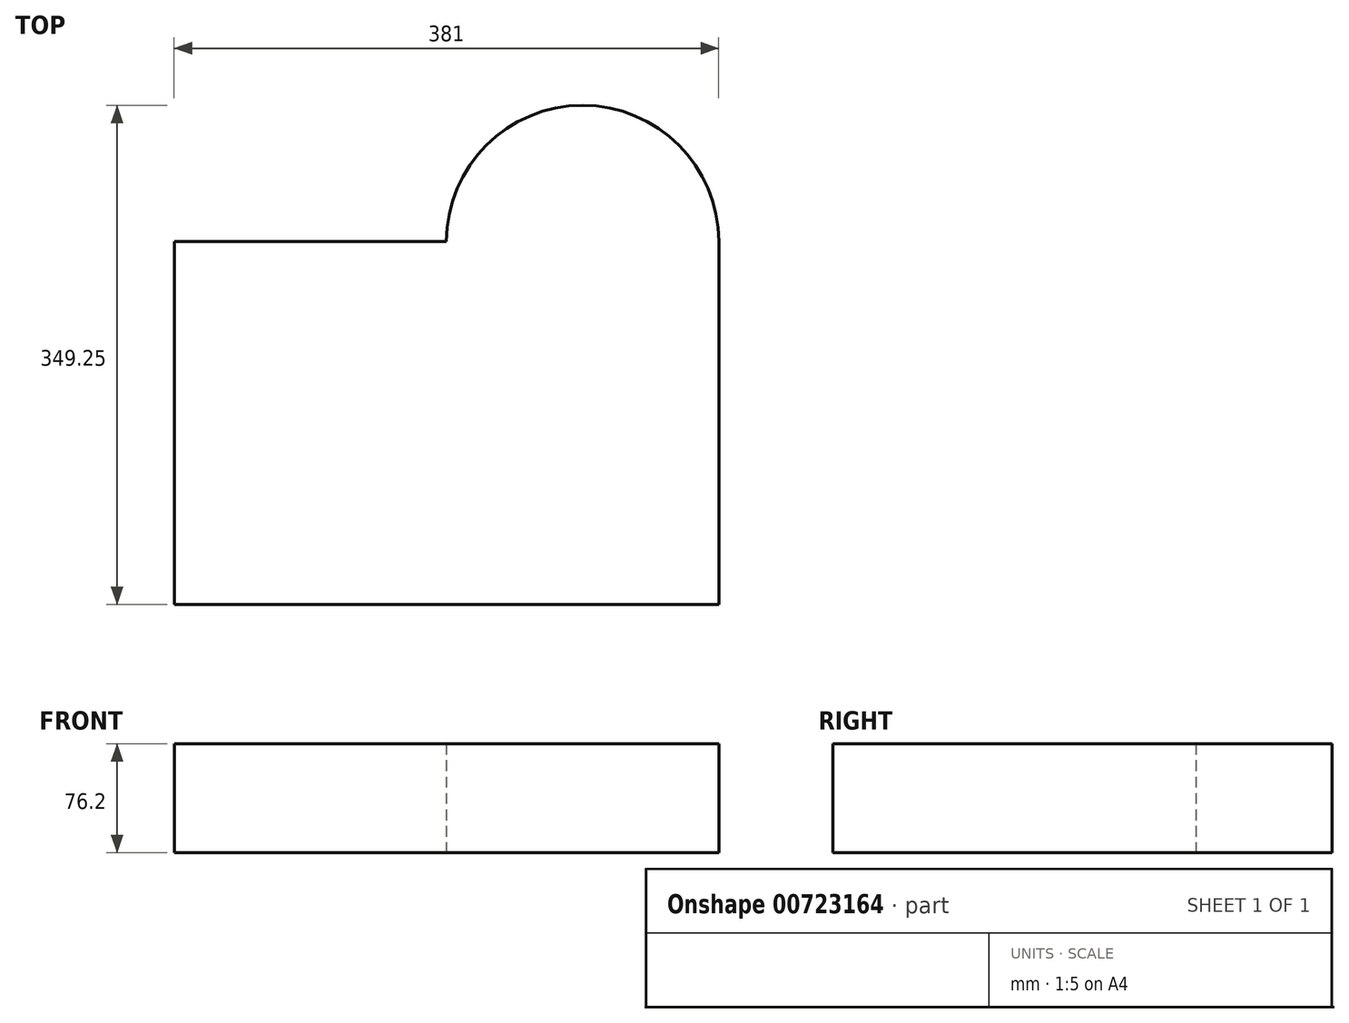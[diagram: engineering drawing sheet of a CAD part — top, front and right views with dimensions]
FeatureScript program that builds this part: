
annotation { "Feature Type Name" : "Feature", "Feature Type Description" : "" }
export const myFeature = defineFeature(function(context is Context, id is Id, definition is map)
    precondition{}
    {
        {
            var Q0;
            Q0=qCreatedBy(makeId("Top.planeOp"),FACE);
            var sketch = newSketch(context, id + "F0", { "sketchPlane" : qUnion([Q0])});
            skLineSegment(sketch, "E0.bottom", {"start": v(201.08, -150.57) * mm, "end": v(-179.92, -150.57) * mm});
            skLineSegment(sketch, "E0.top", {"start": v(201.08, 103.43) * mm, "end": v(-179.92, 103.43) * mm});
            skLineSegment(sketch, "E0.left", {"start": v(201.08, -150.57) * mm, "end": v(201.08, 103.43) * mm});
            skLineSegment(sketch, "E0.right", {"start": v(-179.92, -150.57) * mm, "end": v(-179.92, 103.43) * mm});
            skArc(sketch, "E1", {"start": v(201.08, 103.43) * mm, "mid": v(105.83, 198.68) * mm, "end": v(10.58, 103.43) * mm});
            skSolve(sketch);
        }
        {
            var Q0;
            Q0 = qSketchRegion(id + "F0", true);
            extrude(context, id + "F1", {"entities" : qUnion([Q0]), "depth" : 76.2 * mm, "offsetDistance" : 25.4 * mm});
        }
    });
